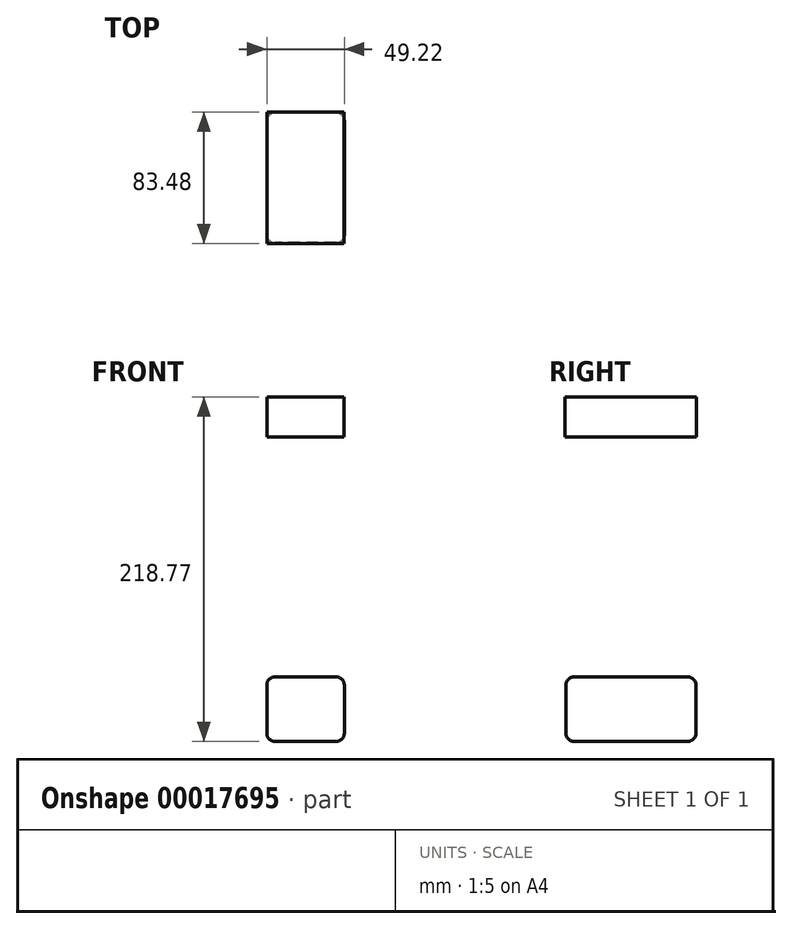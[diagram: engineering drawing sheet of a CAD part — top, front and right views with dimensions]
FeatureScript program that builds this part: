
annotation { "Feature Type Name" : "Feature", "Feature Type Description" : "" }
export const myFeature = defineFeature(function(context is Context, id is Id, definition is map)
    precondition{}
    {
        {
            var Q0;
            Q0=qCreatedBy(makeId("Top.planeOp"),FACE);
            var sketch = newSketch(context, id + "F0", { "sketchPlane" : qUnion([Q0])});
            skLineSegment(sketch, "E0.rect.bottom", {"start": v(24.61, 41.24) * mm, "end": v(-24.61, 41.24) * mm});
            skLineSegment(sketch, "E0.rect.top", {"start": v(24.61, -41.24) * mm, "end": v(-24.61, -41.24) * mm});
            skLineSegment(sketch, "E0.rect.left", {"start": v(24.61, 41.24) * mm, "end": v(24.61, -41.24) * mm});
            skLineSegment(sketch, "E0.rect.right", {"start": v(-24.61, 41.24) * mm, "end": v(-24.61, -41.24) * mm});
            skPoint(sketch, "E0.rect.middle", {"position": v(0, 0) * mm});
            skSolve(sketch);
        }
        {
            var Q0;
            Q0=makeQuery(id+"F0.imprint","IMPRINT",FACE,{"disambiguationData":[TD([[makeQuery(id+"F0.imprint","IMPRINT",EDGE,{"derivedFrom":sQuery(id+"F0.wireOp",EDGE,"E0.rect.bottom")}),1.0]])]});
            extrude(context, id + "F1", {"entities" : qUnion([Q0]), "depth" : 40.97 * mm});
        }
        {
            var Q0;
            Q0=makeQuery(id+"F1.opExtrude","SWEPT_FACE",FACE,{"disambiguationData":[OSD([sQuery(id+"F0.wireOp",EDGE,"E0.rect.left")])]});
            var Q1;
            Q1=makeQuery(id+"F1.opExtrude","SWEPT_FACE",FACE,{"disambiguationData":[OSD([sQuery(id+"F0.wireOp",EDGE,"E0.rect.bottom")])]});
            var Q2;
            Q2=makeQuery(id+"F1.opExtrude","CAP_FACE",FACE,{"disambiguationData":[OSD([sQuery(id+"F0.wireOp",EDGE,"E0.rect.bottom"),sQuery(id+"F0.wireOp",EDGE,"E0.rect.top"),sQuery(id+"F0.wireOp",EDGE,"E0.rect.left"),sQuery(id+"F0.wireOp",EDGE,"E0.rect.right")])],"isStart":false});
            var Q3;
            Q3=makeQuery(id+"F1.opExtrude","SWEPT_FACE",FACE,{"disambiguationData":[OSD([sQuery(id+"F0.wireOp",EDGE,"E0.rect.right")])]});
            var Q4;
            Q4=makeQuery(id+"F1.opExtrude","SWEPT_FACE",FACE,{"disambiguationData":[OSD([sQuery(id+"F0.wireOp",EDGE,"E0.rect.top")])]});
            fillet(context, id + "F2", {"entities" : qUnion([Q0, Q1, Q2, Q3, Q4]), "radius" : 5.08 * mm, "tangentPropagation" : true, "allowEdgeOverflow" : false});
        }
        {
            var Q0;
            Q0=makeQuery(id+"F1.opExtrude","CAP_FACE",FACE,{"disambiguationData":[OSD([sQuery(id+"F0.wireOp",EDGE,"E0.rect.bottom"),sQuery(id+"F0.wireOp",EDGE,"E0.rect.top"),sQuery(id+"F0.wireOp",EDGE,"E0.rect.left"),sQuery(id+"F0.wireOp",EDGE,"E0.rect.right")])],"isStart":false});
            cPlane(context, id + "F3", {"entities" : qUnion([Q0]), "cplaneType" : CPlaneType.OFFSET, "offset" : 152.4 * mm, "width" : 152.4 * mm, "height" : 152.4 * mm});
        }
        {
            var Q0;
            Q0=qCreatedBy(id+"F3.planeOp",FACE);
            var sketch = newSketch(context, id + "F4", { "sketchPlane" : qUnion([Q0])});
            skLineSegment(sketch, "E1.rect.bottom", {"start": v(24.33, 41.74) * mm, "end": v(-24.33, 41.74) * mm});
            skLineSegment(sketch, "E1.rect.top", {"start": v(24.33, -41.74) * mm, "end": v(-24.33, -41.74) * mm});
            skLineSegment(sketch, "E1.rect.left", {"start": v(24.33, 41.74) * mm, "end": v(24.33, -41.74) * mm});
            skLineSegment(sketch, "E1.rect.right", {"start": v(-24.33, 41.74) * mm, "end": v(-24.33, -41.74) * mm});
            skPoint(sketch, "E1.rect.middle", {"position": v(0, 0) * mm});
            skSolve(sketch);
        }
        {
            var Q0;
            Q0=makeQuery(id+"F4.imprint","IMPRINT",FACE,{"disambiguationData":[TD([[makeQuery(id+"F4.imprint","IMPRINT",EDGE,{"derivedFrom":sQuery(id+"F4.wireOp",EDGE,"E1.rect.bottom")}),1.0]])]});
            extrude(context, id + "F5", {"entities" : qUnion([Q0]), "depth" : 25.4 * mm});
        }
    });
